SOLIDWORKS PART (.sldprt)
format: sldprt  version: not decoded by parser v0  size: 250,368 bytes
history: native  units: mm
features: sketch x9, cut_extrude x4, extrude x3, material x1, hole x1 (+12 scaffold rows collapsed)
feature tree (30):
  scaffold x12  (default folders/planes/origin — collapsed)
  material  "Material <not specified>"
  sketch  "Sketch1"  dims[D1=114.3mm D2=55.88mm]
  extrude  "Boss-Extrude1"  Depth=1.651mm
  sketch  "Sketch2"  dims[c1.D1=7.62mm c1.D2=7.62mm c1.D3=7.62mm c1.D4=7.62mm c1.D5=7.62mm c1.D6=7.62mm c1.D7=7.62mm c1.D8=7.62mm c1.D9=4.5212mm c1.D10=2.032mm c1.D11=~5.569145mm c2.D11=2.0]
  cut_extrude  "Cut-Extrude2"  [1 undecoded]
  sketch  "Sketch3"  dims[D1=22.86mm D2=22.86mm]
  extrude  "Boss-Extrude2"  Depth=19.558mm
  sketch  "Sketch7"
  cut_extrude  "Cut-Extrude5"  [1 undecoded]
  sketch  "Sketch8"  dims[D1=~2.444629mm D2=~2.444629mm D3=~2.444629mm D4=~2.444629mm]
  extrude  "Boss-Extrude4"  Depth=6.604mm
  sketch  "Sketch9"  dims[D1=2.54mm]
  cut_extrude  "Cut-Extrude6"  Depth=2.032mm
  sketch  "Sketch10"  dims[D1=~4.96715mm D2=~22.519765mm]
  cut_extrude  "Cut-Extrude7"  Depth=12.7mm
  hole  "CBORE for #0 Binding Head Machine Screw1"  Diameter=1.778mm Depth=8.255025mm
  sketch  "Sketch13"
  sketch  "Sketch12"  dims[hole-wizard template sketch: 42 standard entries collapsed; hole parameters kept: c12.Thru Hole Depth=~8.255025mm c12.C'Bore Dia.=~3.97002mm c12.C'Bore Depth=0.8128mm c12.Near C'Sink Dia.=~5.24002mm c12.D6=~4.399409mm c12.Near C'Sink Angle=90.0deg]
decode coverage: 13 of 17 modeling features carry decoded parameters
note: ~ marks probable driven/reference dimensions
note: 2 parameter values undecoded
note: suppression state not decoded; provenance and decode notes live in map.json
